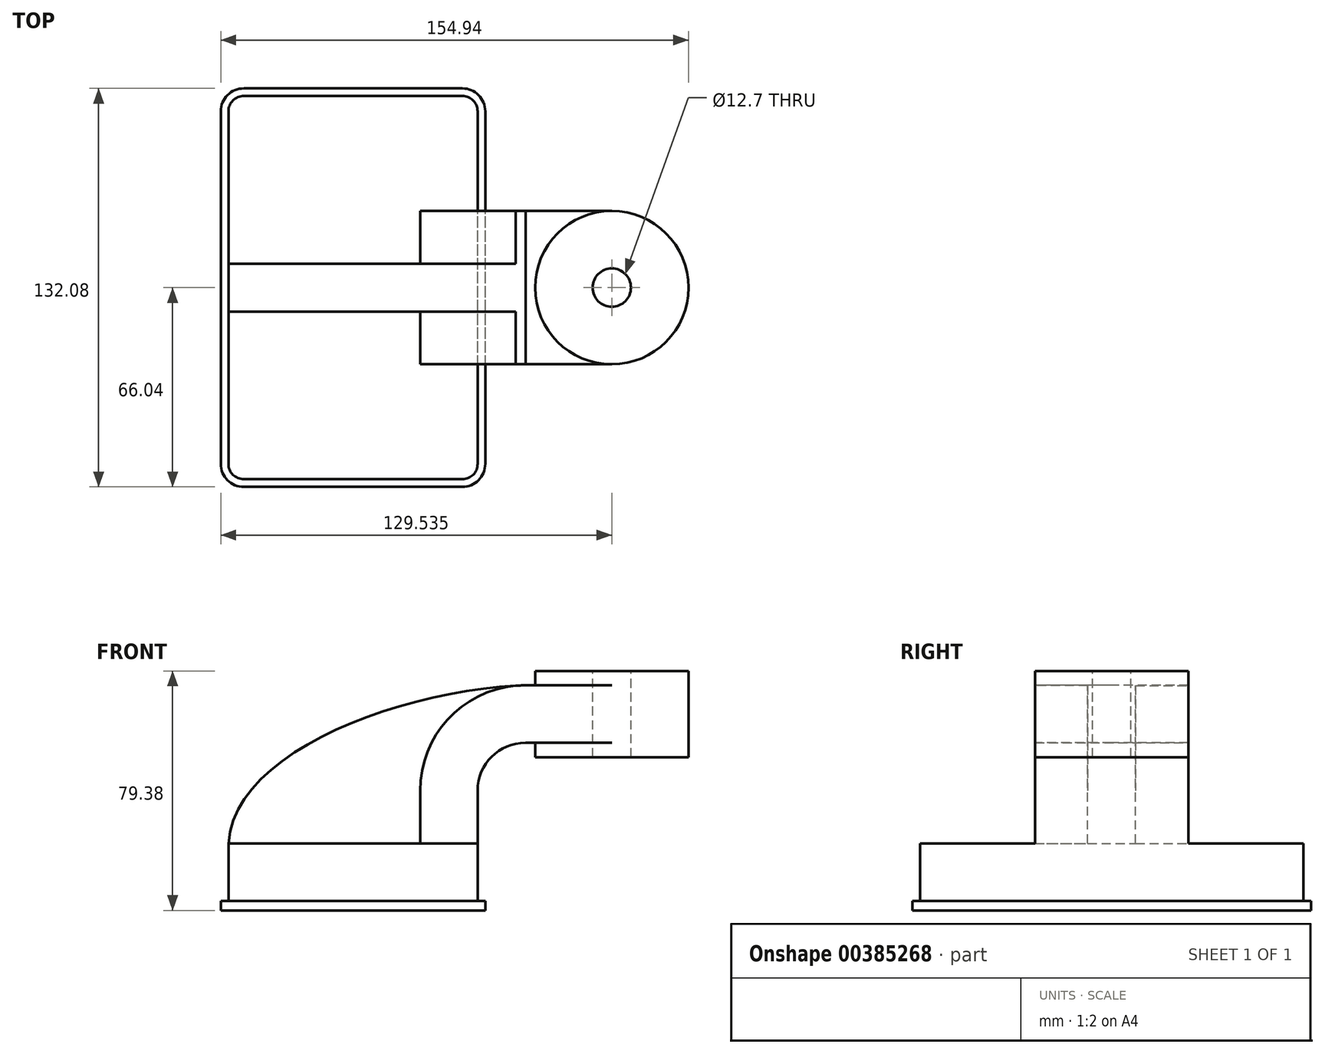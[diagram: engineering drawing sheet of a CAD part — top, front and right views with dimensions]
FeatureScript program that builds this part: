
annotation { "Feature Type Name" : "Feature", "Feature Type Description" : "" }
export const myFeature = defineFeature(function(context is Context, id is Id, definition is map)
    precondition{}
    {
        {
            var Q0;
            Q0=qCreatedBy(makeId("Front.planeOp"),FACE);
            var sketch = newSketch(context, id + "F0", { "sketchPlane" : qUnion([Q0])});
            skLineSegment(sketch, "E0.rect.bottom", {"start": v(-41.28, 9.52) * mm, "end": v(41.28, 9.52) * mm});
            skLineSegment(sketch, "E0.rect.top", {"start": v(-41.28, -9.52) * mm, "end": v(41.28, -9.52) * mm});
            skLineSegment(sketch, "E0.rect.left", {"start": v(-41.28, 9.52) * mm, "end": v(-41.28, -9.52) * mm});
            skLineSegment(sketch, "E0.rect.right", {"start": v(41.28, 9.52) * mm, "end": v(41.28, -9.52) * mm});
            skPoint(sketch, "E0.rect.middle", {"position": v(0, 0) * mm});
            skLineSegment(sketch, "E1", {"start": v(41.28, 9.52) * mm, "end": v(41.28, 27) * mm});
            skArc(sketch, "E2", {"start": v(41.28, 27) * mm, "mid": v(45.92, 38.23) * mm, "end": v(57.15, 42.88) * mm});
            skLineSegment(sketch, "E3", {"start": v(57.15, 42.88) * mm, "end": v(85.72, 42.88) * mm});
            skLineSegment(sketch, "E4.rect.bottom", {"start": v(60.32, 38.1) * mm, "end": v(111.12, 38.1) * mm});
            skLineSegment(sketch, "E4.rect.top", {"start": v(60.32, 66.68) * mm, "end": v(111.12, 66.68) * mm});
            skLineSegment(sketch, "E4.rect.left", {"start": v(60.32, 38.1) * mm, "end": v(60.32, 66.68) * mm});
            skLineSegment(sketch, "E4.rect.right", {"start": v(111.13, 38.1) * mm, "end": v(111.12, 66.68) * mm});
            skPoint(sketch, "E4.rect.middle", {"position": v(85.72, 52.39) * mm});
            skLineSegment(sketch, "E5.0", {"start": v(57.15, 61.93) * mm, "end": v(85.72, 61.93) * mm});
            skArc(sketch, "E5.1", {"start": v(22.23, 27) * mm, "mid": v(32.45, 51.7) * mm, "end": v(57.15, 61.93) * mm});
            skLineSegment(sketch, "E5.2", {"start": v(22.23, 9.52) * mm, "end": v(22.23, 27) * mm});
            skLineSegment(sketch, "E6", {"start": v(85.72, 38.1) * mm, "end": v(85.72, 66.68) * mm});
            skFitSpline(sketch, "E7", {"points": [v(-41.28, 9.53) * mm, v(57.15, 61.93) * mm], "startDerivative": vector(5.2, 92.34) * mm, "endDerivative": vector(120.92, 4.22) * mm});
            skSolve(sketch);
        }
        {
            var Q0;
            Q0=makeQuery(id+"F0.imprint","IMPRINT",FACE,{"disambiguationData":[TD([[makeQuery(id+"F0.imprint","IMPRINT",EDGE,{"derivedFrom":sQuery(id+"F0.wireOp",EDGE,"E0.rect.top")}),1.0]])]});
            extrude(context, id + "F1", {"entities" : qUnion([Q0]), "endBound" : BoundingType.SYMMETRIC, "depth" : 127 * mm});
        }
        {
            var Q0;
            {var subQ9=sQuery(id+"F0.wireOp",EDGE,"E1");Q0=makeQuery(id+"F0.imprint","IMPRINT",FACE,{"disambiguationData":[TD([[makeQuery(id+"F0.imprint","IMPRINT",EDGE,{"derivedFrom":subQ9}),1.0]])]});}
            var Q1;
            {var subQ0=sQuery(id+"F0.wireOp",EDGE,"E6");var subQ1=sQuery(id+"F0.wireOp",EDGE,"E3");var subQ2=makeQuery(id+"F0.imprint","INTERSECT",VERTEX,{"derivedFrom":[subQ1,subQ0]});Q1=makeQuery(id+"F0.imprint","IMPRINT",FACE,{"disambiguationData":[TD([[makeQuery(id+"F0.imprint","IMPRINT",EDGE,{"disambiguationData":[TD([[subQ2,1.0]])],"derivedFrom":subQ1}),1.0]])]});}
            extrude(context, id + "F2", {"entities" : qUnion([Q0, Q1]), "operationType" : NewBodyOperationType.ADD, "endBound" : BoundingType.SYMMETRIC, "depth" : 50.8 * mm});
        }
        {
            var Q0;
            {var subQ3=sQuery(id+"F0.wireOp",EDGE,"E5.2");Q0=makeQuery(id+"F0.imprint","IMPRINT",FACE,{"disambiguationData":[TD([[makeQuery(id+"F0.imprint","IMPRINT",EDGE,{"derivedFrom":subQ3}),1.0]])]});}
            extrude(context, id + "F3", {"entities" : qUnion([Q0]), "operationType" : NewBodyOperationType.ADD, "endBound" : BoundingType.SYMMETRIC, "depth" : 15.88 * mm});
        }
        {
            var Q0;
            {var subQ5=sQuery(id+"F0.wireOp",EDGE,"E4.rect.right");Q0=makeQuery(id+"F0.imprint","IMPRINT",FACE,{"disambiguationData":[TD([[makeQuery(id+"F0.imprint","IMPRINT",EDGE,{"derivedFrom":subQ5}),1.0]])]});}
            var Q1;
            Q1=sQuery(id+"F0.wireOp",EDGE,"E6");
            revolve(context, id + "F4", {"operationType" : NewBodyOperationType.ADD, "entities" : qUnion([Q0]), "axis" : qUnion([Q1]), "revolveType" : RevolveType.FULL});
        }
        {
            var Q0;
            Q0=makeQuery(id+"F1.opExtrude","CAP_EDGE",EDGE,{"disambiguationData":[OSD([sQuery(id+"F0.wireOp",EDGE,"E0.rect.right")])],"isStart":false});
            var Q1;
            Q1=makeQuery(id+"F1.opExtrude","CAP_EDGE",EDGE,{"disambiguationData":[OSD([sQuery(id+"F0.wireOp",EDGE,"E0.rect.left")])],"isStart":false});
            var Q2;
            Q2=makeQuery(id+"F1.opExtrude","CAP_EDGE",EDGE,{"disambiguationData":[OSD([sQuery(id+"F0.wireOp",EDGE,"E0.rect.right")])],"isStart":true});
            var Q3;
            Q3=makeQuery(id+"F1.opExtrude","CAP_EDGE",EDGE,{"disambiguationData":[OSD([sQuery(id+"F0.wireOp",EDGE,"E0.rect.left")])],"isStart":true});
            fillet(context, id + "F5", {"entities" : qUnion([Q0, Q1, Q2, Q3]), "radius" : 5.08 * mm, "tangentPropagation" : true, "allowEdgeOverflow" : false});
        }
        {
            var Q0;
            Q0=makeQuery(id+"F1.opExtrude","SWEPT_FACE",FACE,{"disambiguationData":[OSD([sQuery(id+"F0.wireOp",EDGE,"E0.rect.top")])]});
            var sketch = newSketch(context, id + "F6", { "sketchPlane" : qUnion([Q0])});
            skLineSegment(sketch, "E8.0", {"start": v(-36.2, 66.04) * mm, "end": v(36.2, 66.04) * mm});
            skArc(sketch, "E8.1", {"start": v(43.82, 58.42) * mm, "mid": v(41.58, 63.8) * mm, "end": v(36.2, 66.04) * mm});
            skArc(sketch, "E8.2", {"start": v(-36.2, 66.04) * mm, "mid": v(-41.58, 63.8) * mm, "end": v(-43.82, 58.42) * mm});
            skLineSegment(sketch, "E8.3", {"start": v(43.82, 58.42) * mm, "end": v(43.82, -58.42) * mm});
            skLineSegment(sketch, "E8.4", {"start": v(-43.82, 58.42) * mm, "end": v(-43.82, -58.42) * mm});
            skArc(sketch, "E8.5", {"start": v(-43.82, -58.42) * mm, "mid": v(-41.58, -63.8) * mm, "end": v(-36.2, -66.04) * mm});
            skLineSegment(sketch, "E8.6", {"start": v(-36.2, -66.04) * mm, "end": v(36.2, -66.04) * mm});
            skArc(sketch, "E8.7", {"start": v(36.2, -66.04) * mm, "mid": v(41.58, -63.8) * mm, "end": v(43.82, -58.42) * mm});
            skSolve(sketch);
        }
        {
            var Q0;
            Q0 = qSketchRegion(id + "F6", true);
            extrude(context, id + "F7", {"entities" : qUnion([Q0]), "operationType" : NewBodyOperationType.ADD, "depth" : 3.17 * mm});
        }
        {
            var Q0;
            Q0=makeQuery(id+"F4.opRevolve","SWEPT_FACE",FACE,{"disambiguationData":[OSD([sQuery(id+"F0.wireOp",EDGE,"E4.rect.top")])]});
            var sketch = newSketch(context, id + "F8", { "sketchPlane" : qUnion([Q0])});
            skCircle(sketch, "E9", {"center": v(85.72, 0) * mm, "radius": 6.35 * mm});
            skSolve(sketch);
        }
        {
            var Q0;
            Q0 = qSketchRegion(id + "F8", true);
            extrude(context, id + "F9", {"entities" : qUnion([Q0]), "operationType" : NewBodyOperationType.REMOVE, "endBound" : BoundingType.UP_TO_NEXT, "oppositeDirection" : true, "depth" : 25.4 * mm});
        }
    });
